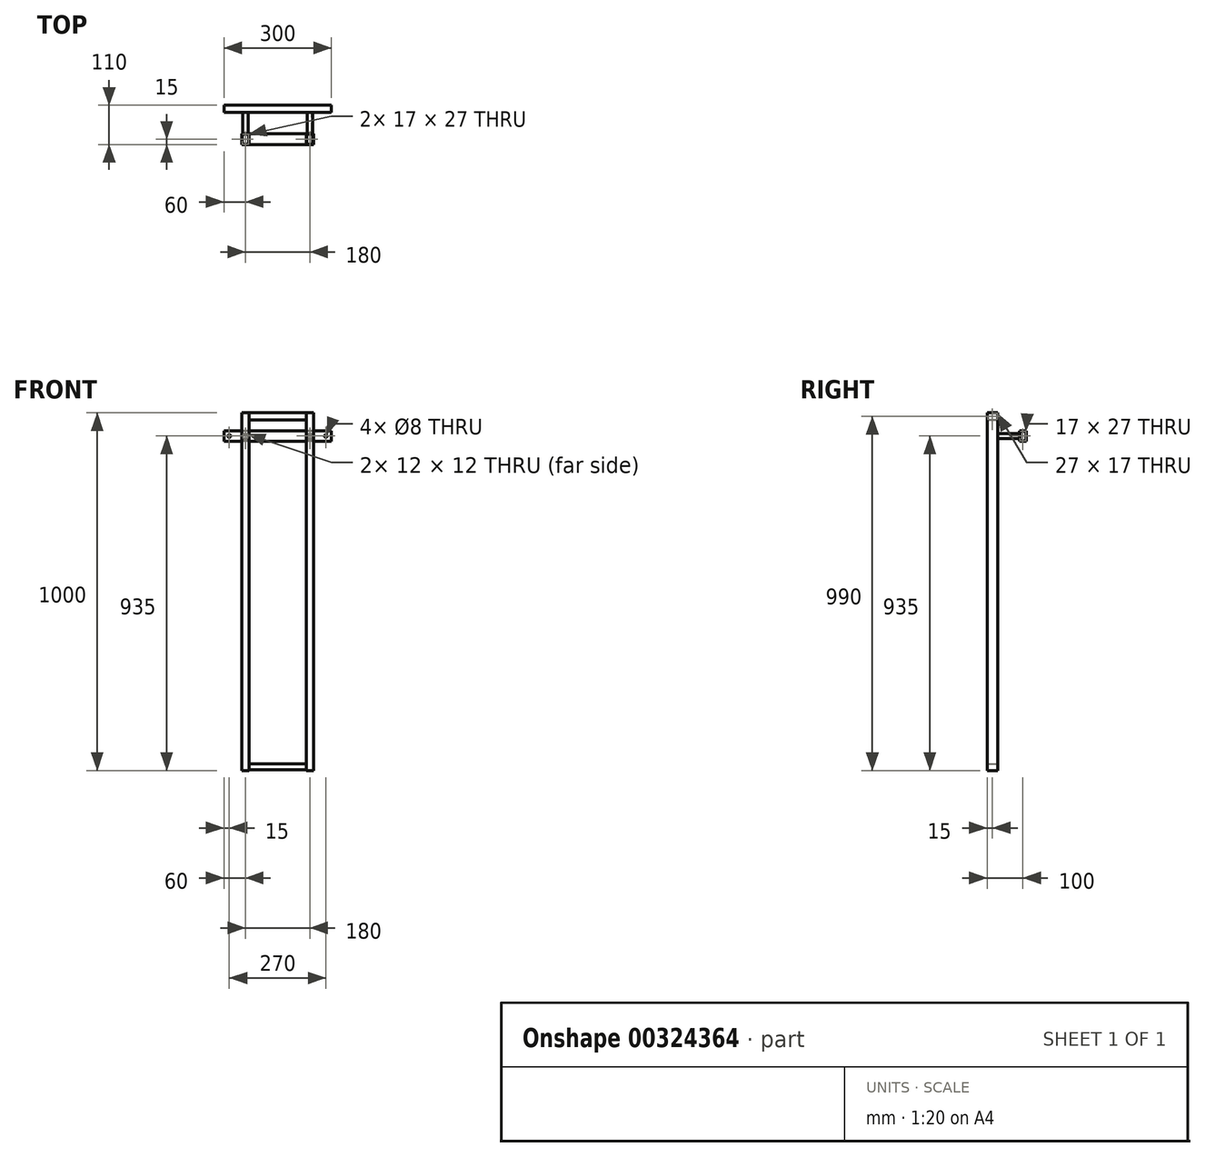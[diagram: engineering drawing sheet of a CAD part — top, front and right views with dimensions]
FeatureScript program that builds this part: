
annotation { "Feature Type Name" : "Feature", "Feature Type Description" : "" }
export const myFeature = defineFeature(function(context is Context, id is Id, definition is map)
    precondition{}
    {
        {
            var Q0;
            Q0=qCreatedBy(makeId("Top.planeOp"),FACE);
            var sketch = newSketch(context, id + "F0", { "sketchPlane" : qUnion([Q0])});
            skLineSegment(sketch, "E0.bottom", {"start": v(-100, 15) * mm, "end": v(-80, 15) * mm});
            skLineSegment(sketch, "E0.top", {"start": v(-100, -15) * mm, "end": v(-80, -15) * mm});
            skLineSegment(sketch, "E0.left", {"start": v(-100, 15) * mm, "end": v(-100, -15) * mm});
            skLineSegment(sketch, "E0.right", {"start": v(-80, 15) * mm, "end": v(-80, -15) * mm});
            skLineSegment(sketch, "E1", {"start": v(0, 0) * mm, "end": v(-80, 0) * mm, "construction": true});
            skLineSegment(sketch, "E2.bottom", {"start": v(-98.5, 13.5) * mm, "end": v(-81.5, 13.5) * mm});
            skLineSegment(sketch, "E2.top", {"start": v(-98.5, -13.5) * mm, "end": v(-81.5, -13.5) * mm});
            skLineSegment(sketch, "E2.left", {"start": v(-98.5, 13.5) * mm, "end": v(-98.5, -13.5) * mm});
            skLineSegment(sketch, "E2.right", {"start": v(-81.5, 13.5) * mm, "end": v(-81.5, -13.5) * mm});
            skLineSegment(sketch, "E3", {"start": v(0, 0) * mm, "end": v(0, 40.25) * mm, "construction": true});
            skLineSegment(sketch, "E4.MirrorCS", {"start": v(80, 15) * mm, "end": v(80, -15) * mm});
            skLineSegment(sketch, "E5.MirrorCS", {"start": v(81.5, 13.5) * mm, "end": v(81.5, -13.5) * mm});
            skLineSegment(sketch, "E6.MirrorCS", {"start": v(98.5, -13.5) * mm, "end": v(81.5, -13.5) * mm});
            skLineSegment(sketch, "E7.MirrorCS", {"start": v(100, -15) * mm, "end": v(80, -15) * mm});
            skLineSegment(sketch, "E8.MirrorCS", {"start": v(100, 15) * mm, "end": v(100, -15) * mm});
            skLineSegment(sketch, "E9.MirrorCS", {"start": v(98.5, 13.5) * mm, "end": v(98.5, -13.5) * mm});
            skLineSegment(sketch, "E10.MirrorCS", {"start": v(98.5, 13.5) * mm, "end": v(81.5, 13.5) * mm});
            skLineSegment(sketch, "E11.MirrorCS", {"start": v(100, 15) * mm, "end": v(80, 15) * mm});
            skSolve(sketch);
        }
        {
            var Q0;
            Q0 = qSketchRegion(id + "F0", true);
            extrude(context, id + "F1", {"entities" : qUnion([Q0]), "endBound" : BoundingType.SYMMETRIC, "depth" : 1000 * mm, "offsetDistance" : 25 * mm});
        }
        {
            var Q0;
            Q0=qCreatedBy(makeId("Right.planeOp"),FACE);
            var sketch = newSketch(context, id + "F2", { "sketchPlane" : qUnion([Q0])});
            skLineSegment(sketch, "E12.bottom", {"start": v(-15, 500) * mm, "end": v(15, 500) * mm});
            skLineSegment(sketch, "E12.top", {"start": v(-15, 480) * mm, "end": v(15, 480) * mm});
            skLineSegment(sketch, "E12.left", {"start": v(-15, 500) * mm, "end": v(-15, 480) * mm});
            skLineSegment(sketch, "E12.right", {"start": v(15, 500) * mm, "end": v(15, 480) * mm});
            skLineSegment(sketch, "E13.bottom", {"start": v(-13.5, 498.5) * mm, "end": v(13.5, 498.5) * mm});
            skLineSegment(sketch, "E13.top", {"start": v(-13.5, 481.5) * mm, "end": v(13.5, 481.5) * mm});
            skLineSegment(sketch, "E13.left", {"start": v(-13.5, 498.5) * mm, "end": v(-13.5, 481.5) * mm});
            skLineSegment(sketch, "E13.right", {"start": v(13.5, 498.5) * mm, "end": v(13.5, 481.5) * mm});
            skLineSegment(sketch, "E14", {"start": v(0, 0) * mm, "end": v(0, 480) * mm, "construction": true});
            skLineSegment(sketch, "E15.0", {"start": v(0, 0) * mm, "end": v(40.25, 0) * mm, "construction": true});
            skLineSegment(sketch, "E16.MirrorCS", {"start": v(-13.5, -481.5) * mm, "end": v(13.5, -481.5) * mm});
            skLineSegment(sketch, "E17.MirrorCS", {"start": v(13.5, -498.5) * mm, "end": v(13.5, -481.5) * mm});
            skLineSegment(sketch, "E18.MirrorCS", {"start": v(-15, -500) * mm, "end": v(15, -500) * mm});
            skLineSegment(sketch, "E19.MirrorCS", {"start": v(-15, -500) * mm, "end": v(-15, -480) * mm});
            skLineSegment(sketch, "E20.MirrorCS", {"start": v(-13.5, -498.5) * mm, "end": v(-13.5, -481.5) * mm});
            skLineSegment(sketch, "E21.MirrorCS", {"start": v(-13.5, -498.5) * mm, "end": v(13.5, -498.5) * mm});
            skSolve(sketch);
        }
        {
            var Q0;
            Q0 = qSketchRegion(id + "F2", true);
            extrude(context, id + "F3", {"entities" : qUnion([Q0]), "endBound" : BoundingType.UP_TO_NEXT, "depth" : 25 * mm, "offsetDistance" : 25 * mm, "hasSecondDirection" : true, "secondDirectionBound" : SecondDirectionBoundingType.UP_TO_NEXT, "secondDirectionOppositeDirection" : true, "secondDirectionDepth" : 25 * mm});
        }
        {
            var Q0;
            Q0=qCreatedBy(makeId("Right.planeOp"),FACE);
            var sketch = newSketch(context, id + "F4", { "sketchPlane" : qUnion([Q0])});
            skLineSegment(sketch, "E22.bottom", {"start": v(75, 420) * mm, "end": v(95, 420) * mm});
            skLineSegment(sketch, "E22.top", {"start": v(75, 450) * mm, "end": v(95, 450) * mm});
            skLineSegment(sketch, "E22.left", {"start": v(75, 420) * mm, "end": v(75, 450) * mm});
            skLineSegment(sketch, "E22.right", {"start": v(95, 420) * mm, "end": v(95, 450) * mm});
            skLineSegment(sketch, "E23.0", {"start": v(76.5, 448.5) * mm, "end": v(93.5, 448.5) * mm});
            skLineSegment(sketch, "E23.1", {"start": v(76.5, 421.5) * mm, "end": v(76.5, 448.5) * mm});
            skLineSegment(sketch, "E23.2", {"start": v(76.5, 421.5) * mm, "end": v(93.5, 421.5) * mm});
            skLineSegment(sketch, "E23.3", {"start": v(93.5, 421.5) * mm, "end": v(93.5, 448.5) * mm});
            skSolve(sketch);
        }
        {
            var Q0;
            Q0 = qSketchRegion(id + "F4", true);
            extrude(context, id + "F5", {"entities" : qUnion([Q0]), "endBound" : BoundingType.SYMMETRIC, "depth" : 300 * mm, "offsetDistance" : 25 * mm});
        }
        {
            var Q0;
            Q0=makeQuery(id+"F5.opExtrude","SWEPT_FACE",FACE,{"disambiguationData":[OSD([sQuery(id+"F4.wireOp",EDGE,"E22.left")])]});
            var sketch = newSketch(context, id + "F6", { "sketchPlane" : qUnion([Q0])});
            skLineSegment(sketch, "E24.bottom", {"start": v(82.5, 442.5) * mm, "end": v(97.5, 442.5) * mm});
            skLineSegment(sketch, "E24.top", {"start": v(82.5, 427.5) * mm, "end": v(97.5, 427.5) * mm});
            skLineSegment(sketch, "E24.left", {"start": v(82.5, 442.5) * mm, "end": v(82.5, 427.5) * mm});
            skLineSegment(sketch, "E24.right", {"start": v(97.5, 442.5) * mm, "end": v(97.5, 427.5) * mm});
            skLineSegment(sketch, "E25", {"start": v(80, 420) * mm, "end": v(100, 420) * mm, "construction": true});
            skLineSegment(sketch, "E26", {"start": v(80, 420) * mm, "end": v(80, 450) * mm, "construction": true});
            skLineSegment(sketch, "E27", {"start": v(80, 435) * mm, "end": v(82.5, 435) * mm, "construction": true});
            skLineSegment(sketch, "E28", {"start": v(90, 427.5) * mm, "end": v(90, 420) * mm, "construction": true});
            skLineSegment(sketch, "E29", {"start": v(80, 450) * mm, "end": v(100, 450) * mm, "construction": true});
            skLineSegment(sketch, "E30", {"start": v(100, 450) * mm, "end": v(100, 420) * mm, "construction": true});
            skLineSegment(sketch, "E31", {"start": v(90, 442.5) * mm, "end": v(90, 450) * mm, "construction": true});
            skLineSegment(sketch, "E32", {"start": v(97.5, 435) * mm, "end": v(100, 435) * mm, "construction": true});
            skLineSegment(sketch, "E33.0", {"start": v(84, 441) * mm, "end": v(96, 441) * mm});
            skLineSegment(sketch, "E33.1", {"start": v(84, 441) * mm, "end": v(84, 429) * mm});
            skLineSegment(sketch, "E33.2", {"start": v(84, 429) * mm, "end": v(96, 429) * mm});
            skLineSegment(sketch, "E33.3", {"start": v(96, 441) * mm, "end": v(96, 429) * mm});
            skLineSegment(sketch, "E34", {"start": v(0, 450) * mm, "end": v(0, 420) * mm, "construction": true});
            skLineSegment(sketch, "E35.MirrorCS", {"start": v(-82.5, 442.5) * mm, "end": v(-82.5, 427.5) * mm});
            skLineSegment(sketch, "E36.MirrorCS", {"start": v(-82.5, 442.5) * mm, "end": v(-97.5, 442.5) * mm});
            skLineSegment(sketch, "E37.MirrorCS", {"start": v(-97.5, 442.5) * mm, "end": v(-97.5, 427.5) * mm});
            skLineSegment(sketch, "E38.MirrorCS", {"start": v(-82.5, 427.5) * mm, "end": v(-97.5, 427.5) * mm});
            skLineSegment(sketch, "E39.MirrorCS", {"start": v(-84, 429) * mm, "end": v(-96, 429) * mm});
            skLineSegment(sketch, "E40.MirrorCS", {"start": v(-96, 441) * mm, "end": v(-96, 429) * mm});
            skLineSegment(sketch, "E41.MirrorCS", {"start": v(-84, 441) * mm, "end": v(-96, 441) * mm});
            skLineSegment(sketch, "E42.MirrorCS", {"start": v(-84, 441) * mm, "end": v(-84, 429) * mm});
            skSolve(sketch);
        }
        {
            var Q0;
            Q0 = qSketchRegion(id + "F6", true);
            extrude(context, id + "F7", {"entities" : qUnion([Q0]), "endBound" : BoundingType.UP_TO_NEXT, "depth" : 25 * mm, "offsetDistance" : 25 * mm});
        }
        {
            var Q0;
            Q0=makeQuery(id+"F5.opExtrude","SWEPT_FACE",FACE,{"disambiguationData":[OSD([sQuery(id+"F4.wireOp",EDGE,"E22.left")])]});
            var sketch = newSketch(context, id + "F8", { "sketchPlane" : qUnion([Q0])});
            skCircle(sketch, "E43", {"center": v(135, 435) * mm, "radius": 4 * mm});
            skLineSegment(sketch, "E44", {"start": v(150, 435) * mm, "end": v(135, 435) * mm, "construction": true});
            skLineSegment(sketch, "E45", {"start": v(0, 450) * mm, "end": v(0, 420) * mm, "construction": true});
            skCircle(sketch, "E46.MirrorC", {"center": v(-135, 435) * mm, "radius": 4 * mm});
            skSolve(sketch);
        }
        {
            var Q0;
            Q0=sQuery(id+"F8.wireOp",VERTEX,"E43.center");
            var Q1;
            Q1=sQuery(id+"F8.wireOp",VERTEX,"E46.MirrorC.center");
            var Q2;
            Q2=makeQuery(id+"F5.opExtrude","SWEPT_BODY",BODY,{"disambiguationData":[OSD([sQuery(id+"F4.wireOp",EDGE,"E22.bottom"),sQuery(id+"F4.wireOp",EDGE,"E22.top"),sQuery(id+"F4.wireOp",EDGE,"E22.left"),sQuery(id+"F4.wireOp",EDGE,"E22.right"),sQuery(id+"F4.wireOp",EDGE,"E23.0"),sQuery(id+"F4.wireOp",EDGE,"E23.1"),sQuery(id+"F4.wireOp",EDGE,"E23.2"),sQuery(id+"F4.wireOp",EDGE,"E23.3")])]});
            hole(context, id + "F9", {"style" : HoleStyle.SIMPLE, "endStyle" : HoleEndStyle.THROUGH, "holeDiameter" : 8 * mm, "majorDiameter" : 5 * mm, "isTappedThrough" : true, "tappedDepth" : 12 * mm, "tapClearance" : 3, "locations" : qUnion([Q0, Q1]), "scope" : qUnion([Q2])});
        }
    });
